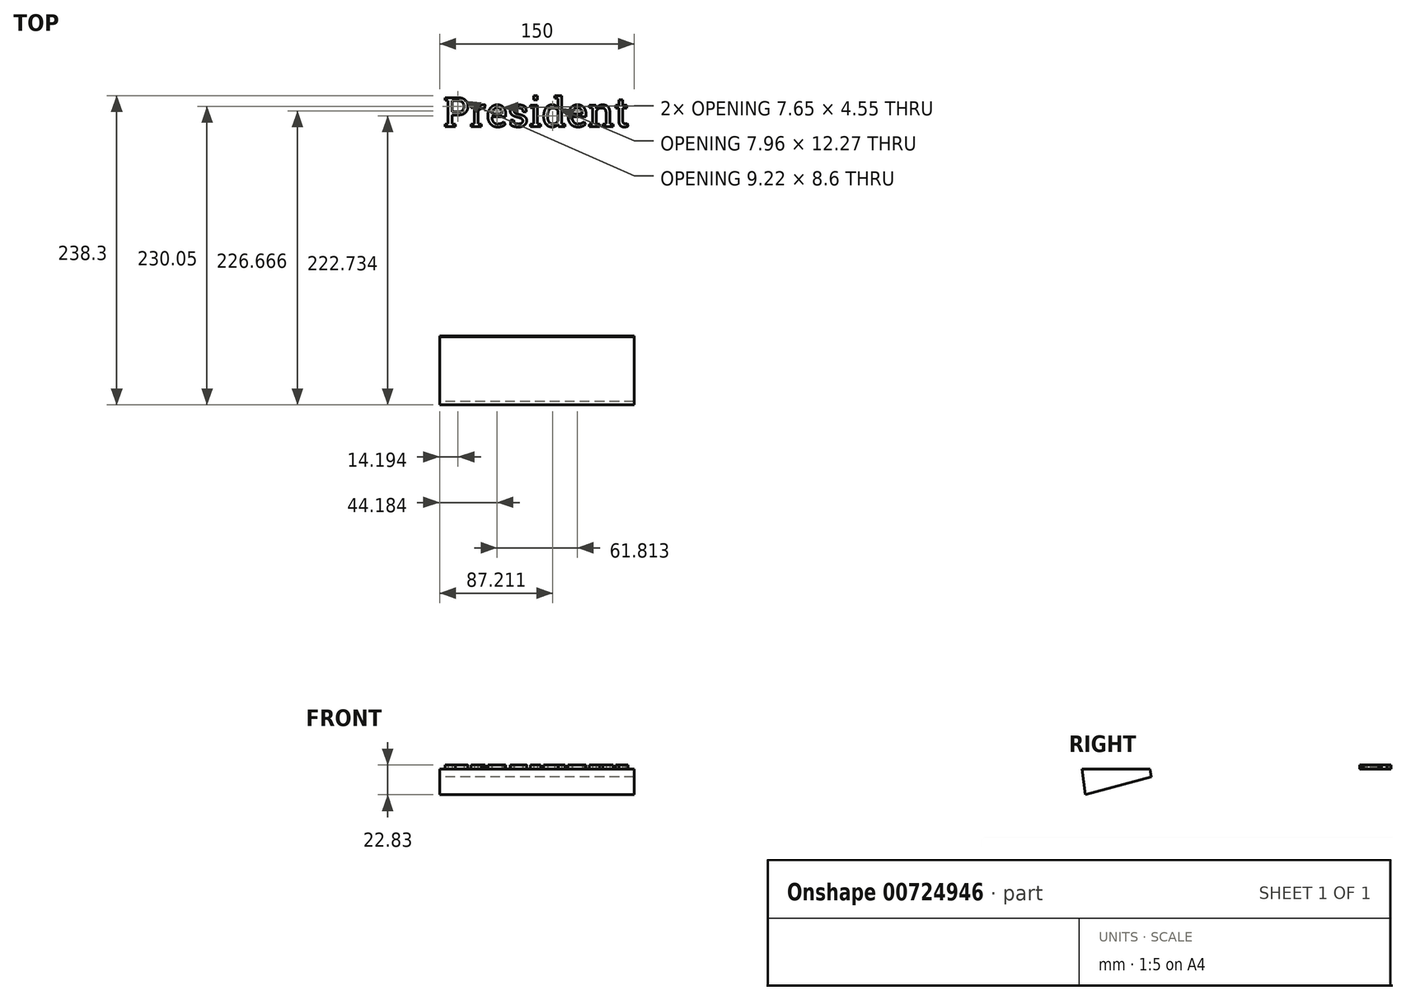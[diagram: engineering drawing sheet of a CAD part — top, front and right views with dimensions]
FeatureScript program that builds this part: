
annotation { "Feature Type Name" : "Feature", "Feature Type Description" : "" }
export const myFeature = defineFeature(function(context is Context, id is Id, definition is map)
    precondition{}
    {
        {
            var Q0;
            Q0=qCreatedBy(makeId("Right.planeOp"),FACE);
            var sketch = newSketch(context, id + "F0", { "sketchPlane" : qUnion([Q0])});
            skLineSegment(sketch, "E0", {"start": v(-139.6, 29.47) * mm, "end": v(-191.14, 22.53) * mm, "construction": true});
            skLineSegment(sketch, "E1", {"start": v(-191.14, 22.53) * mm, "end": v(-192.48, 32.45) * mm});
            skLineSegment(sketch, "E2", {"start": v(-192.48, 32.45) * mm, "end": v(-140, 32.45) * mm});
            skLineSegment(sketch, "E3", {"start": v(-140, 32.45) * mm, "end": v(-139.6, 29.47) * mm});
            skLineSegment(sketch, "E4.MirrorCS", {"start": v(-139.2, 26.5) * mm, "end": v(-139.6, 29.47) * mm});
            skLineSegment(sketch, "E5.MirrorCS", {"start": v(-189.8, 12.62) * mm, "end": v(-139.2, 26.5) * mm});
            skLineSegment(sketch, "E6.MirrorCS", {"start": v(-189.8, 12.62) * mm, "end": v(-191.14, 22.53) * mm});
            skSolve(sketch);
        }
        {
            var Q0;
            Q0=makeQuery(id+"F0.imprint","IMPRINT",FACE,{"disambiguationData":[TD([[makeQuery(id+"F0.imprint","IMPRINT",EDGE,{"derivedFrom":sQuery(id+"F0.wireOp",EDGE,"E1")}),-1.0]])]});
            extrude(context, id + "F1", {"entities" : qUnion([Q0]), "depth" : 75 * mm, "offsetDistance" : 25.4 * mm, "hasSecondDirection" : true, "secondDirectionOppositeDirection" : true, "secondDirectionDepth" : 75 * mm});
        }
        {
            var Q0;
            Q0=makeQuery(id+"F1.opExtrude","SWEPT_FACE",FACE,{"disambiguationData":[OSD([sQuery(id+"F0.wireOp",EDGE,"E2")])]});
            var sketch = newSketch(context, id + "F2", { "sketchPlane" : qUnion([Q0])});
            skText(sketch, "E7", { "text": "President", "fontName": "RobotoSlab-Regular.ttf"});
            skLineSegment(sketch, "E8", {"start": v(7.89, -140) * mm, "end": v(7.89, -154.98) * mm, "construction": true});
            skLineSegment(sketch, "E9", {"start": v(11.59, -177.5) * mm, "end": v(11.59, -192.48) * mm, "construction": true});
            const initialGuessF2  = {"E7": [-0.072, 0.022, 1, 0, 0.02252]};
            skSetInitialGuess(sketch, initialGuessF2);
            skSolve(sketch);
        }
        {
            var Q0;
            Q0 = qSketchRegion(id + "F2", true);
            extrude(context, id + "F3", {"entities" : qUnion([Q0]), "operationType" : NewBodyOperationType.ADD, "depth" : 3 * mm, "offsetDistance" : 25 * mm});
        }
    });
